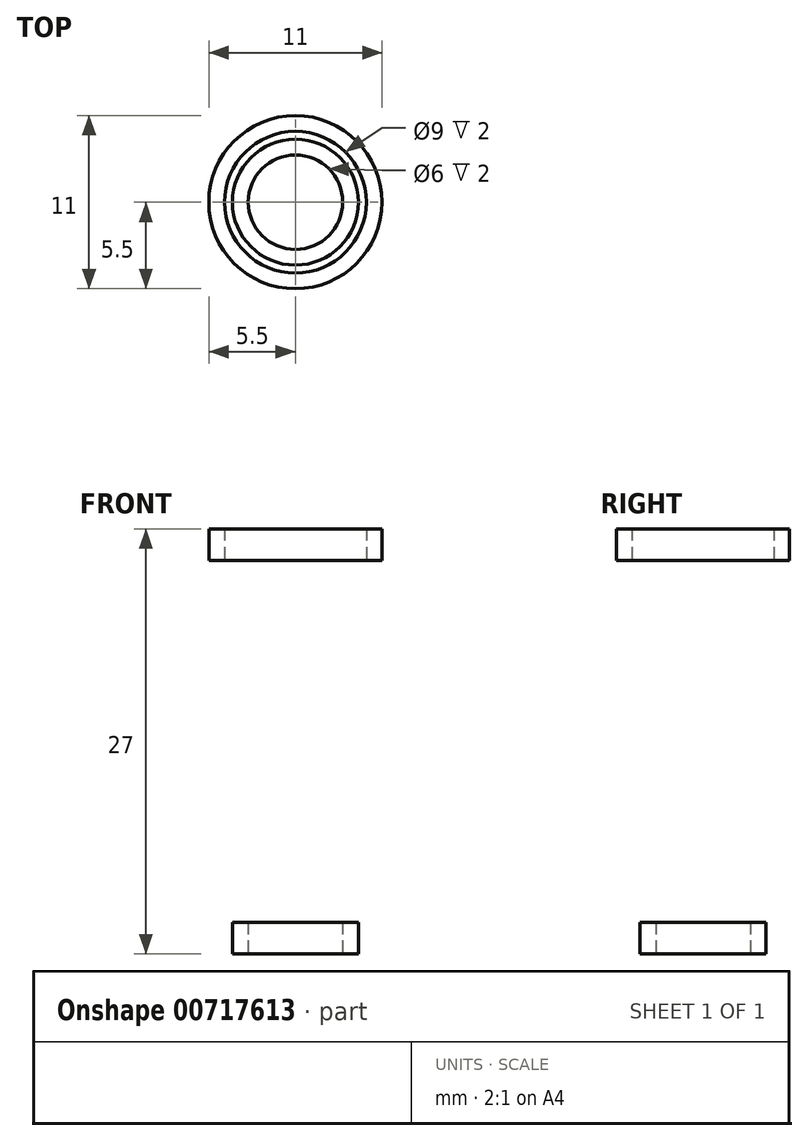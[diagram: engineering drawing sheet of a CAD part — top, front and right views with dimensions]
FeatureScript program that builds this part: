
annotation { "Feature Type Name" : "Feature", "Feature Type Description" : "" }
export const myFeature = defineFeature(function(context is Context, id is Id, definition is map)
    precondition{}
    {
        {
            var Q0;
            Q0=qCreatedBy(makeId("Top.planeOp"),FACE);
            var sketch = newSketch(context, id + "F0", { "sketchPlane" : qUnion([Q0])});
            skCircle(sketch, "E0", {"center": v(0, 0) * mm, "radius": 3 * mm});
            skCircle(sketch, "E1", {"center": v(0, 0) * mm, "radius": 4 * mm});
            skSolve(sketch);
        }
        {
            var Q0;
            Q0=makeQuery(id+"F0.imprint","IMPRINT",FACE,{"disambiguationData":[TD([[makeQuery(id+"F0.imprint","IMPRINT",EDGE,{"derivedFrom":sQuery(id+"F0.wireOp",EDGE,"E0")}),-1.0]])]});
            extrude(context, id + "F1", {"entities" : qUnion([Q0]), "depth" : 2 * mm, "offsetDistance" : 25 * mm});
        }
        {
            var Q0;
            Q0=qCreatedBy(makeId("Top.planeOp"),FACE);
            cPlane(context, id + "F2", {"entities" : qUnion([Q0]), "cplaneType" : CPlaneType.OFFSET, "offset" : 25 * mm, "width" : 150 * mm, "height" : 150 * mm});
        }
        {
            var Q0;
            Q0=qCreatedBy(id+"F2.planeOp",FACE);
            var sketch = newSketch(context, id + "F3", { "sketchPlane" : qUnion([Q0])});
            skCircle(sketch, "E2", {"center": v(0, 0) * mm, "radius": 4.5 * mm});
            skCircle(sketch, "E3", {"center": v(0, 0) * mm, "radius": 5.5 * mm});
            skSolve(sketch);
        }
        {
            var Q0;
            Q0=makeQuery(id+"F3.imprint","IMPRINT",FACE,{"disambiguationData":[TD([[makeQuery(id+"F3.imprint","IMPRINT",EDGE,{"derivedFrom":sQuery(id+"F3.wireOp",EDGE,"E2")}),-1.0]])]});
            var Q1;
            Q1 = qConstructionFilter(qBodyType(qCreatedBy(id + "F3" ,EDGE), BodyType.WIRE), ConstructionObject.NO);
            extrude(context, id + "F4", {"entities" : qUnion([Q0]), "surfaceEntities" : qUnion([Q1]), "depth" : 2 * mm, "offsetDistance" : 25 * mm});
        }
    });
